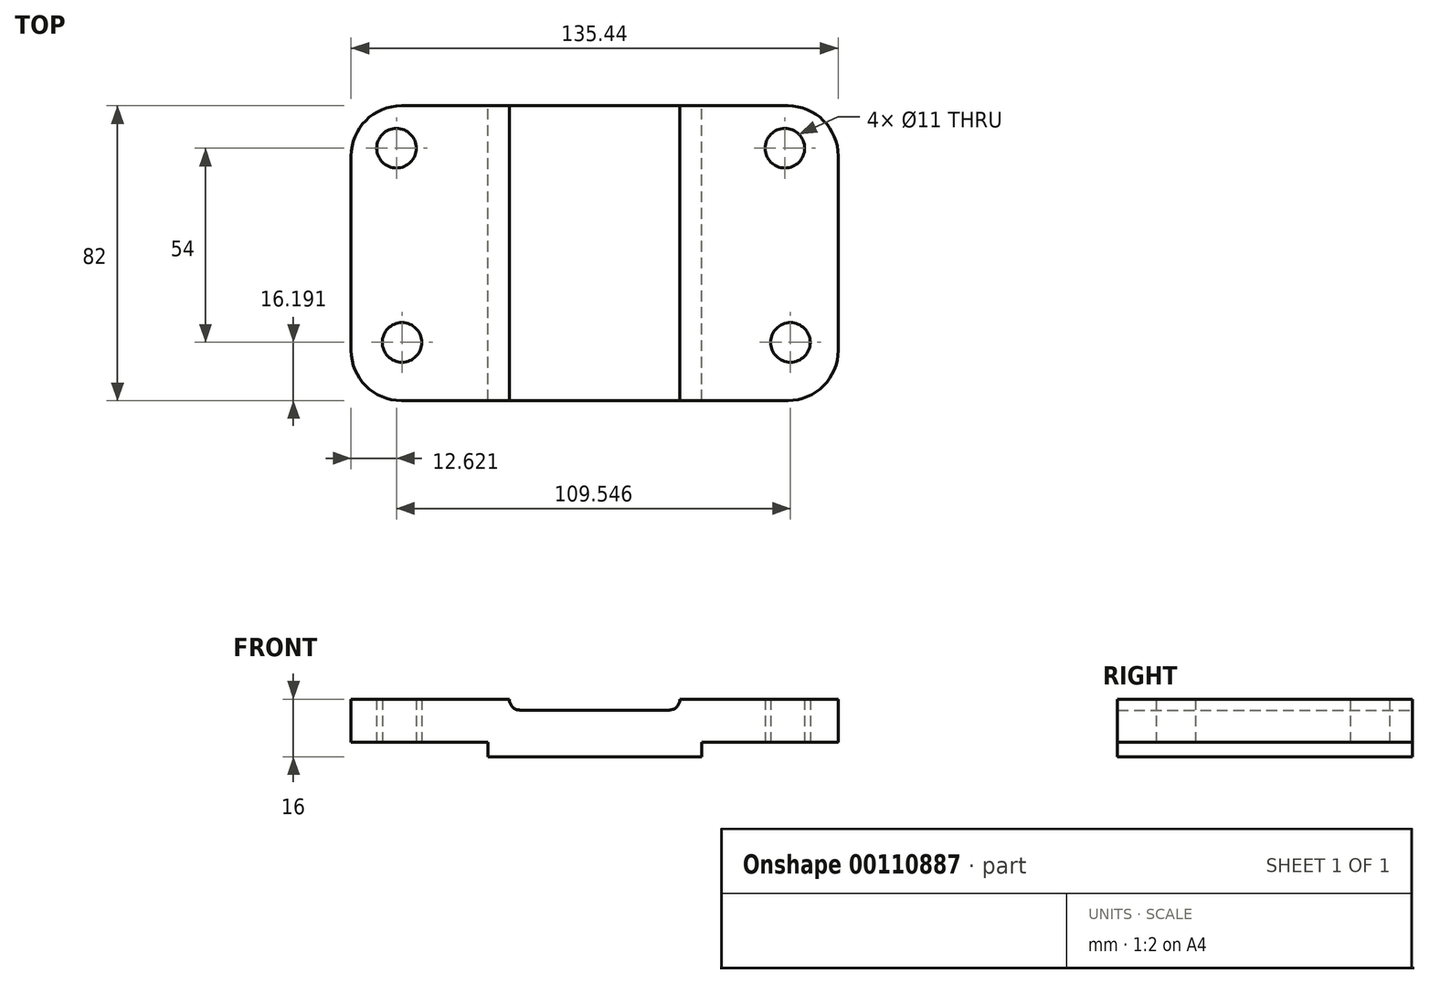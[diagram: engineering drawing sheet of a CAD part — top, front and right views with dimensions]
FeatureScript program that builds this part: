
annotation { "Feature Type Name" : "Feature", "Feature Type Description" : "" }
export const myFeature = defineFeature(function(context is Context, id is Id, definition is map)
    precondition{}
    {
        {
            var Q0;
            Q0=qCreatedBy(makeId("Front.planeOp"),FACE);
            var sketch = newSketch(context, id + "F0", { "sketchPlane" : qUnion([Q0])});
            skLineSegment(sketch, "E0", {"start": v(0, 0) * mm, "end": v(38, 0) * mm});
            skLineSegment(sketch, "E1", {"start": v(38, 0) * mm, "end": v(38, -4) * mm});
            skLineSegment(sketch, "E2", {"start": v(38, -4) * mm, "end": v(97.44, -4) * mm});
            skLineSegment(sketch, "E3", {"start": v(97.44, -4) * mm, "end": v(97.44, 0) * mm});
            skLineSegment(sketch, "E4", {"start": v(97.44, 0) * mm, "end": v(135.44, 0) * mm});
            skLineSegment(sketch, "E5", {"start": v(135.44, 0) * mm, "end": v(135.44, 12) * mm});
            skLineSegment(sketch, "E6", {"start": v(135.44, 12) * mm, "end": v(91.44, 12) * mm});
            skLineSegment(sketch, "E7", {"start": v(44, 12) * mm, "end": v(0, 12) * mm});
            skLineSegment(sketch, "E8", {"start": v(0, 12) * mm, "end": v(0, 0) * mm});
            skLineSegment(sketch, "E9", {"start": v(91.44, 12) * mm, "end": v(91.44, 11.95) * mm});
            skLineSegment(sketch, "E10", {"start": v(88.44, 8.95) * mm, "end": v(47, 8.95) * mm});
            skLineSegment(sketch, "E11", {"start": v(44, 11.92) * mm, "end": v(44, 12) * mm});
            skPoint(sketch, "E12.visualSharp", {"position": v(91.44, 8.95) * mm});
            skArc(sketch, "E12.filletArc", {"start": v(88.44, 8.95) * mm, "mid": v(90.56, 9.82) * mm, "end": v(91.44, 11.95) * mm});
            skPoint(sketch, "E13.visualSharp", {"position": v(44.03, 8.95) * mm});
            skArc(sketch, "E13.filletArc", {"start": v(44, 11.92) * mm, "mid": v(44.89, 9.81) * mm, "end": v(47, 8.95) * mm});
            skSolve(sketch);
        }
        {
            var Q0;
            Q0 = qSketchRegion(id + "F0", true);
            extrude(context, id + "F1", {"entities" : qUnion([Q0]), "depth" : 82 * mm});
        }
        {
            var Q0;
            Q0=qCreatedBy(makeId("Top.planeOp"),FACE);
            var sketch = newSketch(context, id + "F2", { "sketchPlane" : qUnion([Q0])});
            skCircle(sketch, "E14", {"center": v(12.62, -11.8) * mm, "radius": 5.5 * mm});
            skCircle(sketch, "E15", {"center": v(120.62, -11.8) * mm, "radius": 5.5 * mm});
            skCircle(sketch, "E16", {"center": v(14.17, -65.8) * mm, "radius": 5.5 * mm});
            skCircle(sketch, "E17", {"center": v(122.17, -65.8) * mm, "radius": 5.5 * mm});
            skSolve(sketch);
        }
        {
            var Q0;
            Q0 = qSketchRegion(id + "F2", true);
            extrude(context, id + "F3", {"entities" : qUnion([Q0]), "operationType" : NewBodyOperationType.REMOVE, "endBound" : BoundingType.THROUGH_ALL, "depth" : 25.4 * mm});
        }
        {
            var Q0;
            Q0=makeQuery(id+"F1.opExtrude","CAP_EDGE",EDGE,{"disambiguationData":[OSD([sQuery(id+"F0.wireOp",EDGE,"E5")])],"isStart":true});
            var Q1;
            Q1=makeQuery(id+"F1.opExtrude","CAP_EDGE",EDGE,{"disambiguationData":[OSD([sQuery(id+"F0.wireOp",EDGE,"E5")])],"isStart":false});
            var Q2;
            Q2=makeQuery(id+"F1.opExtrude","CAP_EDGE",EDGE,{"disambiguationData":[OSD([sQuery(id+"F0.wireOp",EDGE,"E8")])],"isStart":false});
            var Q3;
            Q3=makeQuery(id+"F1.opExtrude","CAP_EDGE",EDGE,{"disambiguationData":[OSD([sQuery(id+"F0.wireOp",EDGE,"E8")])],"isStart":true});
            fillet(context, id + "F4", {"entities" : qUnion([Q0, Q1, Q2, Q3]), "radius" : 14 * mm, "tangentPropagation" : true, "allowEdgeOverflow" : false});
        }
    });
